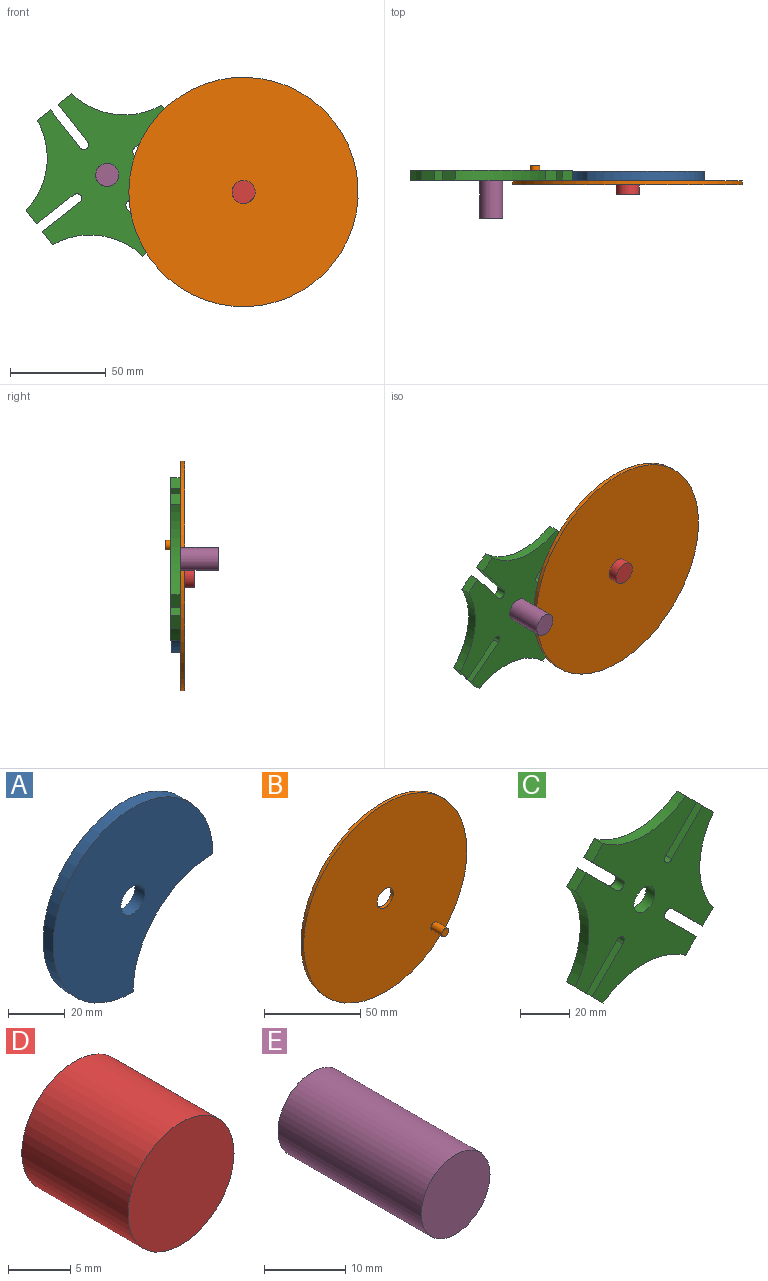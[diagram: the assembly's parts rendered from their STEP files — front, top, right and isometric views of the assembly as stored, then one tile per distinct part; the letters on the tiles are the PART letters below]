
ASSEMBLY  parts=5 mates=3
PART A: 5 faces, bbox 80x5x80 mm
  f0: cylinder r=6mm len=12mm, axis (0,1,0), area 188.5mm2, adj f2,f3
  f1: cylinder r=40mm len=80mm, axis (0,1,0), area 942.5mm2, adj f2,f3,f4
  f2: plane 80x80mm, normal (0,-1,0), area 4000.2mm2, adj f0,f1,f4
  f3: plane 80x80mm, normal (0,1,0), area 4000.2mm2, adj f0,f1,f4
  f4: cylinder r=40mm len=40mm, axis (0,-1,0), area 314.2mm2, adj f1,f2,f3
PART B: 6 faces, bbox 120x10x120 mm
  f0: cylinder r=6mm len=12mm, axis (0,1,0), area 75.4mm2, adj f2,f3
  f1: cylinder r=60mm len=120mm, axis (0,1,0), area 754mm2, adj f2,f3
  f2: plane 120x120mm, normal (0,-1,0), area 11177mm2, adj f0,f1,f4
  f3: plane 120x120mm, normal (0,1,0), area 11196.6mm2, adj f0,f1
  f4: cylinder r=2.5mm len=8mm, axis (0,1,0), area 125.7mm2, adj f2,f5
  f5: plane 5x5mm, normal (0,-1,0), area 19.6mm2, adj f4
PART C: 27 faces, bbox 79.6x5x79.6 mm
  f0: plane 6.23x6.23mm, normal (-0.71,0,-0.71), area 44.1mm2, adj f1,f24,f25,f26
  f1: cylinder r=40mm len=47.63mm, axis (0,1,0), area 255.1mm2, adj f0,f2,f25,f26
  f2: plane 6.23x6.23mm, normal (0.71,0,-0.71), area 44.1mm2, adj f1,f3,f25,f26
  f3: plane 17.68x17.68mm, normal (0.71,0,0.71), area 125mm2, adj f2,f4,f25,f26
  f4: cylinder r=2.5mm len=5mm, axis (0,1,0), area 39.3mm2, adj f3,f5,f25,f26
  f5: plane 17.68x17.68mm, normal (-0.71,0,-0.71), area 125mm2, adj f4,f6,f25,f26
  f6: plane 6.23x6.23mm, normal (0.71,0,-0.71), area 44.1mm2, adj f5,f7,f25,f26
  f7: cylinder r=40mm len=47.65mm, axis (0,1,0), area 255.2mm2, adj f6,f8,f25,f26
  f8: plane 6.23x6.23mm, normal (0.71,0,0.71), area 44.1mm2, adj f7,f9,f25,f26
  f9: plane 17.68x17.68mm, normal (-0.71,0,0.71), area 125mm2, adj f8,f10,f25,f26
  f10: cylinder r=2.5mm len=5mm, axis (0,1,0), area 39.3mm2, adj f9,f11,f25,f26
  f11: plane 17.68x17.68mm, normal (0.71,0,-0.71), area 125mm2, adj f10,f12,f25,f26
  f12: plane 6.23x6.23mm, normal (0.71,0,0.71), area 44.1mm2, adj f11,f13,f25,f26
  f13: cylinder r=40mm len=47.63mm, axis (0,1,0), area 255.1mm2, adj f12,f14,f25,f26
  f14: plane 6.23x6.23mm, normal (-0.71,0,0.71), area 44.1mm2, adj f13,f15,f25,f26
  f15: plane 17.68x17.68mm, normal (-0.71,0,-0.71), area 125mm2, adj f14,f16,f25,f26
  f16: cylinder r=2.5mm len=5mm, axis (0,1,0), area 39.3mm2, adj f15,f17,f25,f26
  f17: plane 17.68x17.68mm, normal (0.71,0,0.71), area 125mm2, adj f16,f18,f25,f26
  f18: plane 6.23x6.23mm, normal (-0.71,0,0.71), area 44.1mm2, adj f17,f19,f25,f26
  f19: cylinder r=40mm len=47.65mm, axis (0,1,0), area 255.2mm2, adj f18,f20,f25,f26
  f20: plane 6.23x6.23mm, normal (-0.71,0,-0.71), area 44.1mm2, adj f19,f21,f25,f26
  f21: plane 17.68x17.68mm, normal (0.71,0,-0.71), area 125mm2, adj f20,f22,f25,f26
  f22: cylinder r=2.5mm len=5mm, axis (0,1,0), area 39.3mm2, adj f21,f24,f25,f26
  f23: cylinder r=6mm len=12mm, axis (0,1,0), area 188.5mm2, adj f25,f26
  f24: plane 17.68x17.68mm, normal (-0.71,0,0.71), area 125mm2, adj f0,f22,f25,f26
  f25: plane 79.64x79.64mm, normal (0,-1,0), area 4157.4mm2, adj f0,f1,f2,f3,f4,f5,f6,f7
  f26: plane 79.64x79.64mm, normal (0,1,0), area 4157.4mm2, adj f0,f1,f2,f3,f4,f5,f6,f7
PART D: 3 faces, bbox 12x12x12 mm
  f0: cylinder r=6mm len=12mm, axis (0,1,0), area 452.4mm2, adj f1,f2
  f1: plane 12x12mm, normal (0,-1,0), area 113.1mm2, adj f0
  f2: plane 12x12mm, normal (0,1,0), area 113.1mm2, adj f0
PART E: 3 faces, bbox 12x25x12 mm
  f0: cylinder r=6mm len=25mm, axis (0,1,0), area 942.5mm2, adj f1,f2
  f1: plane 12x12mm, normal (0,-1,0), area 113.1mm2, adj f0
  f2: plane 12x12mm, normal (0,1,0), area 113.1mm2, adj f0
PLACE A rot(axis=(-0.49,0,-0.87),180deg) t=(-70.61,-173.73,177.54)mm
PLACE B rot(axis=(-0.53,0,-0.85),180deg) t=(-70.7,-175.73,177.57)mm
PLACE C rot(axis=(0,1,0),97.2deg) t=(-142.01,-168.33,186.5)mm
PLACE D rot(axis=(0,1,0),128.4deg) t=(-70.61,-174.73,177.54)mm fixed
PLACE E rot(axis=(0,1,0),30.7deg) t=(-142.01,-168.33,186.5)mm fixed
MATE revolute C.f23 <-> E.f0  axis (0,1,0) through (-142.01,-168.33,186.5)mm
MATE parallel C.f23 <-> B.f0  axis (0,-1,0) through (-142.01,-173.33,186.5)mm
MATE revolute D.f0 <-> A.f0  axis (0,1,0) through (-70.61,-168.73,177.54)mm
